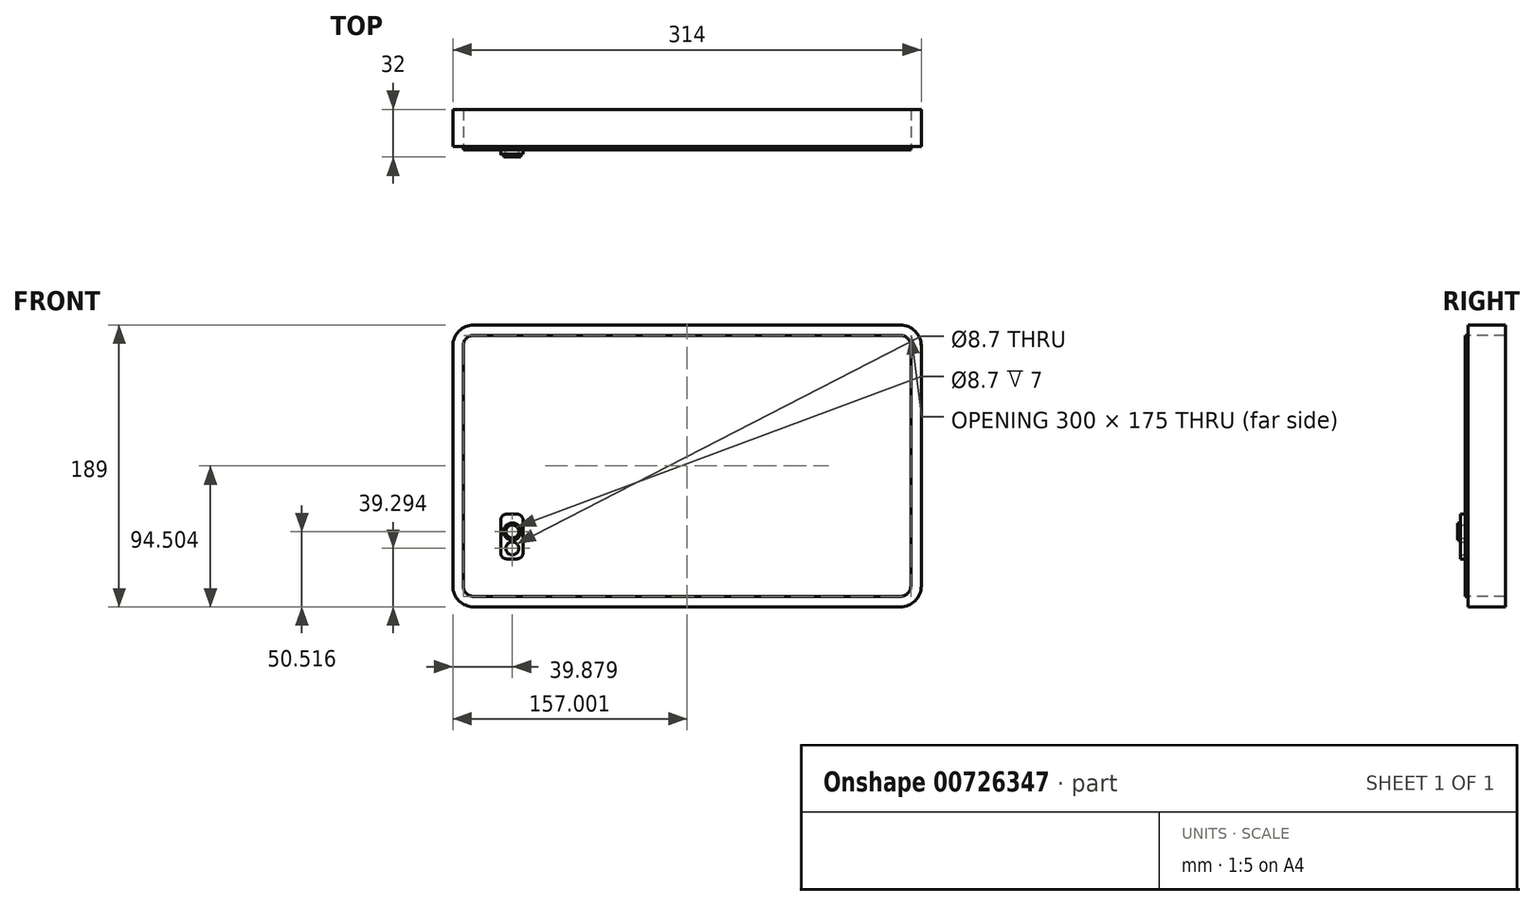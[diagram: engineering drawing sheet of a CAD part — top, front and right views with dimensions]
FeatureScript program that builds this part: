
annotation { "Feature Type Name" : "Feature", "Feature Type Description" : "" }
export const myFeature = defineFeature(function(context is Context, id is Id, definition is map)
    precondition{}
    {
        {
            var Q0;
            Q0=qCreatedBy(makeId("Front.planeOp"),FACE);
            var sketch = newSketch(context, id + "F0", { "sketchPlane" : qUnion([Q0])});
            skLineSegment(sketch, "E0.bottom", {"start": v(-140.03, 80.17) * mm, "end": v(145.97, 80.17) * mm});
            skLineSegment(sketch, "E0.top", {"start": v(-140.03, -94.83) * mm, "end": v(145.97, -94.83) * mm});
            skLineSegment(sketch, "E0.left", {"start": v(-147.03, 73.17) * mm, "end": v(-147.03, -87.83) * mm});
            skLineSegment(sketch, "E0.right", {"start": v(152.97, 73.17) * mm, "end": v(152.97, -87.83) * mm});
            skPoint(sketch, "E1.visualSharp", {"position": v(-147.03, 80.17) * mm});
            skArc(sketch, "E1.filletArc", {"start": v(-140.03, 80.17) * mm, "mid": v(-144.98, 78.12) * mm, "end": v(-147.03, 73.17) * mm});
            skPoint(sketch, "E2.visualSharp", {"position": v(-147.03, -94.83) * mm});
            skArc(sketch, "E2.filletArc", {"start": v(-147.03, -87.83) * mm, "mid": v(-144.98, -92.78) * mm, "end": v(-140.03, -94.83) * mm});
            skPoint(sketch, "E3.visualSharp", {"position": v(152.97, -94.83) * mm});
            skArc(sketch, "E3.filletArc", {"start": v(145.97, -94.83) * mm, "mid": v(150.92, -92.78) * mm, "end": v(152.97, -87.83) * mm});
            skPoint(sketch, "E4.visualSharp", {"position": v(152.97, 80.17) * mm});
            skArc(sketch, "E4.filletArc", {"start": v(152.97, 73.17) * mm, "mid": v(150.92, 78.12) * mm, "end": v(145.97, 80.17) * mm});
            skArc(sketch, "E5.0", {"start": v(-140.03, 87.17) * mm, "mid": v(-149.93, 83.07) * mm, "end": v(-154.03, 73.17) * mm});
            skLineSegment(sketch, "E5.1", {"start": v(-154.03, 73.17) * mm, "end": v(-154.03, -87.83) * mm});
            skLineSegment(sketch, "E5.2", {"start": v(-140.03, 87.17) * mm, "end": v(145.97, 87.17) * mm});
            skArc(sketch, "E5.3", {"start": v(-154.03, -87.83) * mm, "mid": v(-149.93, -97.73) * mm, "end": v(-140.03, -101.83) * mm});
            skArc(sketch, "E5.4", {"start": v(159.97, 73.17) * mm, "mid": v(155.87, 83.07) * mm, "end": v(145.97, 87.17) * mm});
            skLineSegment(sketch, "E5.5", {"start": v(159.97, 73.17) * mm, "end": v(159.97, -87.83) * mm});
            skArc(sketch, "E5.6", {"start": v(145.97, -101.83) * mm, "mid": v(155.87, -97.73) * mm, "end": v(159.97, -87.83) * mm});
            skLineSegment(sketch, "E5.7", {"start": v(-140.03, -101.83) * mm, "end": v(145.97, -101.83) * mm});
            skLineSegment(sketch, "E6.bottom", {"start": v(-117.9, -39.62) * mm, "end": v(-110.9, -39.62) * mm});
            skLineSegment(sketch, "E6.top", {"start": v(-117.9, -69.62) * mm, "end": v(-110.9, -69.62) * mm});
            skLineSegment(sketch, "E6.left", {"start": v(-121.9, -43.62) * mm, "end": v(-121.9, -65.62) * mm});
            skLineSegment(sketch, "E6.right", {"start": v(-106.9, -43.62) * mm, "end": v(-106.9, -65.62) * mm});
            skPoint(sketch, "E7.visualSharp", {"position": v(-121.9, -39.62) * mm});
            skArc(sketch, "E7.filletArc", {"start": v(-117.9, -39.62) * mm, "mid": v(-120.73, -40.8) * mm, "end": v(-121.9, -43.62) * mm});
            skPoint(sketch, "E8.visualSharp", {"position": v(-106.9, -39.62) * mm});
            skArc(sketch, "E8.filletArc", {"start": v(-106.9, -43.62) * mm, "mid": v(-108.07, -40.8) * mm, "end": v(-110.9, -39.62) * mm});
            skPoint(sketch, "E9.visualSharp", {"position": v(-106.9, -69.62) * mm});
            skArc(sketch, "E9.filletArc", {"start": v(-110.9, -69.62) * mm, "mid": v(-108.07, -68.45) * mm, "end": v(-106.9, -65.62) * mm});
            skPoint(sketch, "E10.visualSharp", {"position": v(-121.9, -69.62) * mm});
            skArc(sketch, "E10.filletArc", {"start": v(-121.9, -65.62) * mm, "mid": v(-120.73, -68.45) * mm, "end": v(-117.9, -69.62) * mm});
            skCircle(sketch, "E11", {"center": v(-114.15, -62.54) * mm, "radius": 4.35 * mm});
            skCircle(sketch, "E12", {"center": v(-114.15, -51.31) * mm, "radius": 4.35 * mm});
            skCircle(sketch, "E13.0", {"center": v(-114.15, -51.31) * mm, "radius": 5.75 * mm});
            skSolve(sketch);
        }
        {
            var Q0;
            Q0=makeQuery(id+"F0.imprint","IMPRINT",FACE,{"disambiguationData":[TD([[makeQuery(id+"F0.imprint","IMPRINT",EDGE,{"derivedFrom":sQuery(id+"F0.wireOp",EDGE,"E0.bottom")}),1.0]])]});
            extrude(context, id + "F1", {"entities" : qUnion([Q0]), "depth" : -25 * mm, "offsetDistance" : 25 * mm});
        }
        {
            var Q0;
            Q0=makeQuery(id+"F0.imprint","IMPRINT",FACE,{"disambiguationData":[TD([[makeQuery(id+"F0.imprint","IMPRINT",EDGE,{"derivedFrom":sQuery(id+"F0.wireOp",EDGE,"E0.bottom")}),-1.0]])]});
            extrude(context, id + "F2", {"entities" : qUnion([Q0]), "operationType" : NewBodyOperationType.ADD, "depth" : 2 * mm, "offsetDistance" : 25 * mm});
        }
        {
            var Q0;
            Q0=makeQuery(id+"F0.imprint","IMPRINT",FACE,{"disambiguationData":[TD([[makeQuery(id+"F0.imprint","IMPRINT",EDGE,{"derivedFrom":sQuery(id+"F0.wireOp",EDGE,"E6.bottom")}),-1.0]])]});
            var Q1;
            Q1=makeQuery(id+"F0.imprint","IMPRINT",FACE,{"disambiguationData":[TD([[makeQuery(id+"F0.imprint","IMPRINT",EDGE,{"derivedFrom":sQuery(id+"F0.wireOp",EDGE,"E12")}),-1.0]])]});
            extrude(context, id + "F3", {"entities" : qUnion([Q0, Q1]), "operationType" : NewBodyOperationType.ADD, "depth" : 5 * mm, "offsetDistance" : 25 * mm});
        }
        {
            var Q0;
            Q0=makeQuery(id+"F0.imprint","IMPRINT",FACE,{"disambiguationData":[TD([[makeQuery(id+"F0.imprint","IMPRINT",EDGE,{"derivedFrom":sQuery(id+"F0.wireOp",EDGE,"E12")}),-1.0]])]});
            extrude(context, id + "F4", {"entities" : qUnion([Q0]), "operationType" : NewBodyOperationType.ADD, "depth" : 7 * mm, "offsetDistance" : 25 * mm});
        }
    });
